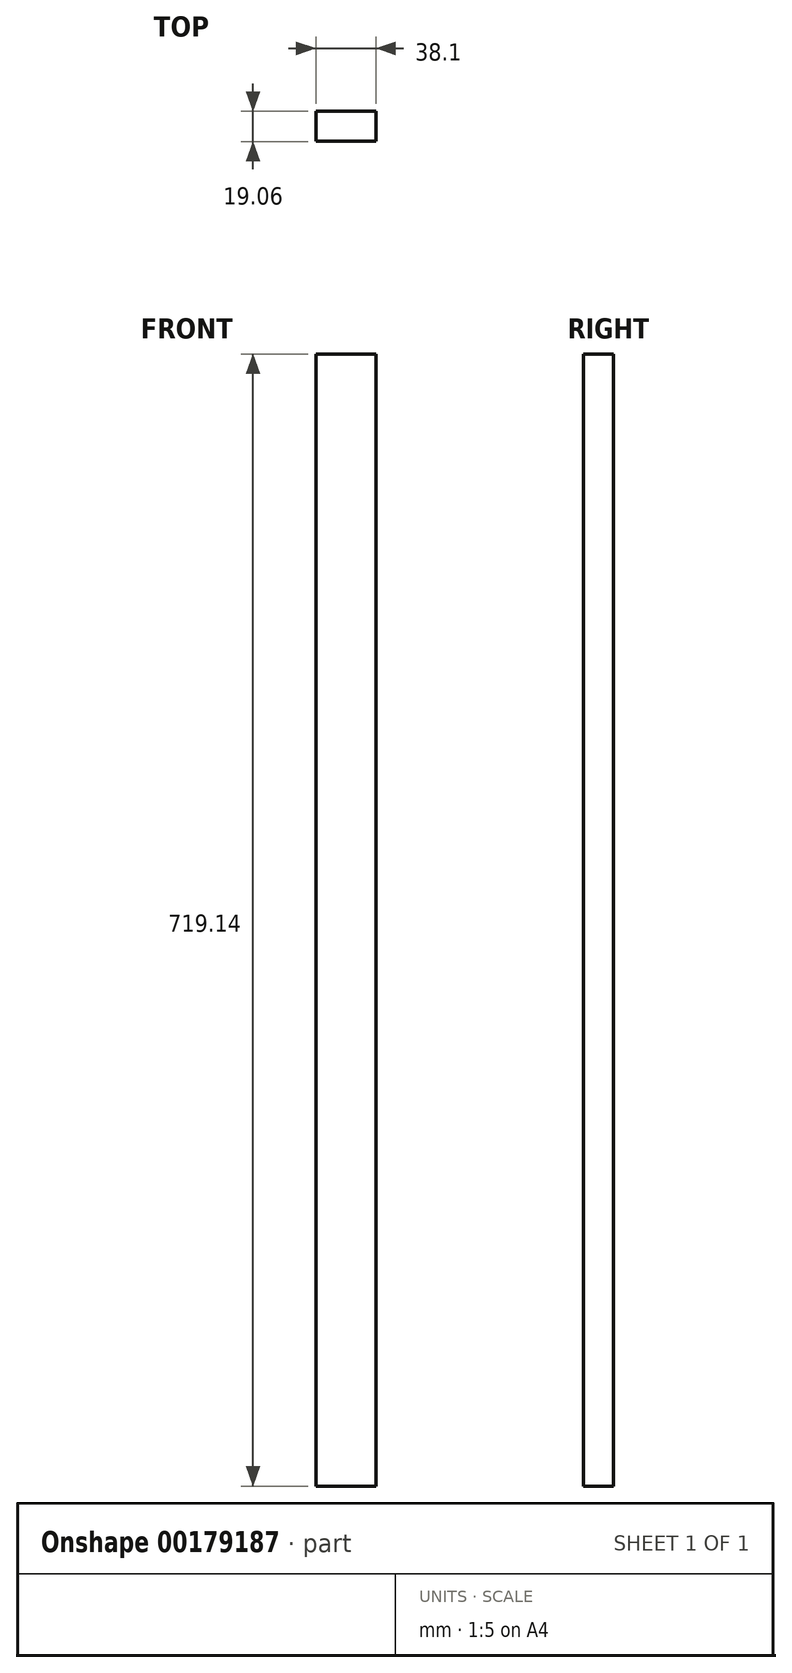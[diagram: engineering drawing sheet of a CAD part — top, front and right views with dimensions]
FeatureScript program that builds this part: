
annotation { "Feature Type Name" : "Feature", "Feature Type Description" : "" }
export const myFeature = defineFeature(function(context is Context, id is Id, definition is map)
    precondition{}
    {
        {
            var Q0;
            Q0=qCreatedBy(makeId("Front.planeOp"),FACE);
            var sketch = newSketch(context, id + "F0", { "sketchPlane" : qUnion([Q0])});
            skLineSegment(sketch, "E0.bottom", {"start": v(-32, 359.57) * mm, "end": v(6.1, 359.57) * mm});
            skLineSegment(sketch, "E0.top", {"start": v(-32, -359.57) * mm, "end": v(6.1, -359.57) * mm});
            skLineSegment(sketch, "E0.left", {"start": v(-32, 359.57) * mm, "end": v(-32, -359.57) * mm});
            skLineSegment(sketch, "E0.right", {"start": v(6.1, 359.57) * mm, "end": v(6.1, -359.57) * mm});
            skLineSegment(sketch, "E1", {"start": v(-32, 0) * mm, "end": v(6.1, 0) * mm});
            skSolve(sketch);
        }
        {
            var Q0;
            {var subQ0=sQuery(id+"F0.wireOp",EDGE,"E0.bottom");Q0=makeQuery(id+"F0.imprint","IMPRINT",FACE,{"disambiguationData":[TD([[makeQuery(id+"F0.imprint","IMPRINT",EDGE,{"derivedFrom":subQ0}),-1.0]])]});}
            var Q1;
            {var subQ0=sQuery(id+"F0.wireOp",EDGE,"E0.top");Q1=makeQuery(id+"F0.imprint","IMPRINT",FACE,{"disambiguationData":[TD([[makeQuery(id+"F0.imprint","IMPRINT",EDGE,{"derivedFrom":subQ0}),1.0]])]});}
            extrude(context, id + "F1", {"entities" : qUnion([Q0, Q1]), "depth" : 19.05 * mm, "symmetric" : true});
        }
    });
